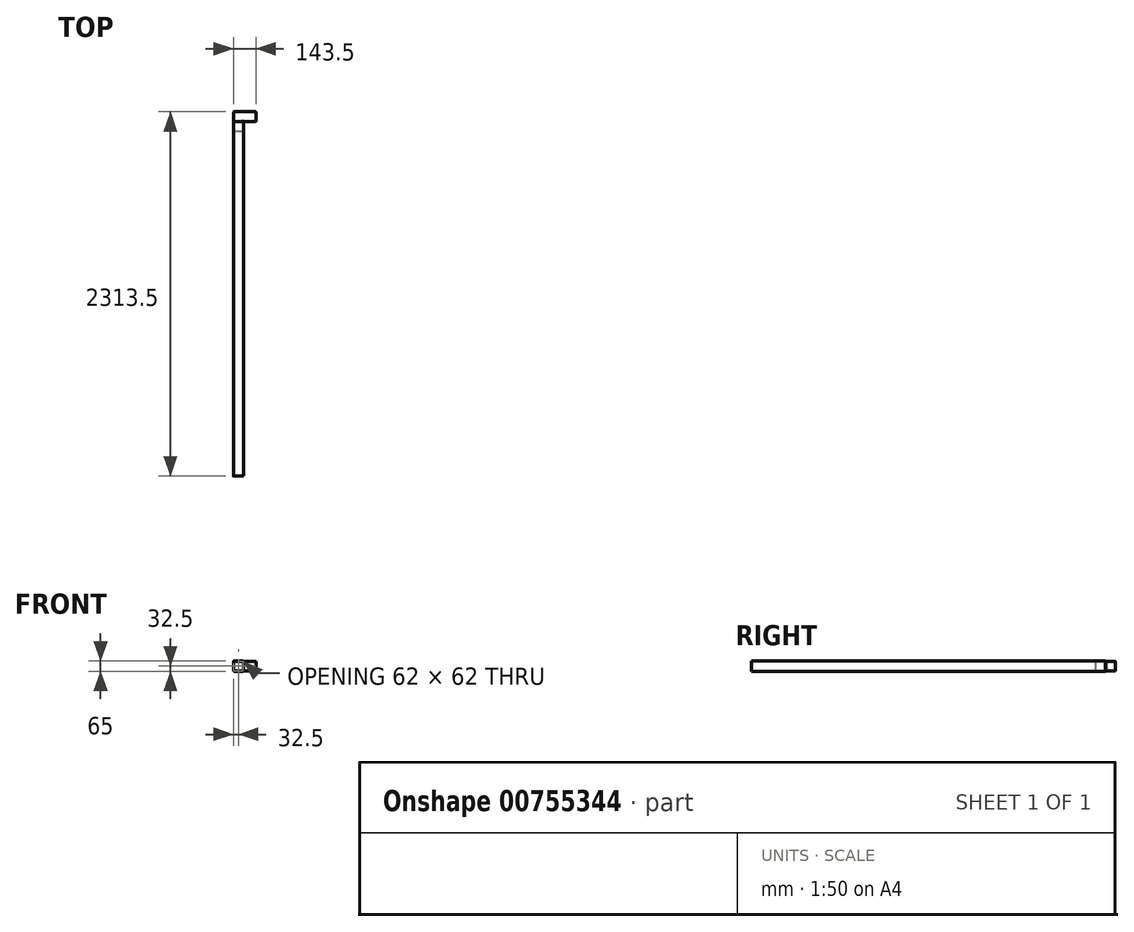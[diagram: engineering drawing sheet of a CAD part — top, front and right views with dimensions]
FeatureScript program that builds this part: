
annotation { "Feature Type Name" : "Feature", "Feature Type Description" : "" }
export const myFeature = defineFeature(function(context is Context, id is Id, definition is map)
    precondition{}
    {
        {
            assignVariable(context, id + "F0", {"name" : "T", "anyValue" : 1.5});
        }
        {
            assignVariable(context, id + "F1", {"name" : "R", "anyValue" : 5});
        }
        {
            var Q0;
            Q0=qCreatedBy(makeId("Front.planeOp"),FACE);
            var sketch = newSketch(context, id + "F2", { "sketchPlane" : qUnion([Q0])});
            skLineSegment(sketch, "E0.bottom", {"start": v(27.5, 32.5) * mm, "end": v(-27.5, 32.5) * mm});
            skLineSegment(sketch, "E0.top", {"start": v(27.5, -32.5) * mm, "end": v(-27.5, -32.5) * mm});
            skLineSegment(sketch, "E0.left", {"start": v(32.5, 27.5) * mm, "end": v(32.5, -27.5) * mm});
            skLineSegment(sketch, "E0.right", {"start": v(-32.5, 27.5) * mm, "end": v(-32.5, -27.5) * mm});
            skPoint(sketch, "E0.middle", {"position": v(0, 0) * mm});
            skPoint(sketch, "E1.visualSharp", {"position": v(-32.5, 32.5) * mm});
            skArc(sketch, "E1.filletArc", {"start": v(-27.5, 32.5) * mm, "mid": v(-31.04, 31.04) * mm, "end": v(-32.5, 27.5) * mm});
            skPoint(sketch, "E2.visualSharp", {"position": v(32.5, 32.5) * mm});
            skArc(sketch, "E2.filletArc", {"start": v(32.5, 27.5) * mm, "mid": v(31.04, 31.04) * mm, "end": v(27.5, 32.5) * mm});
            skPoint(sketch, "E3.visualSharp", {"position": v(32.5, -32.5) * mm});
            skArc(sketch, "E3.filletArc", {"start": v(27.5, -32.5) * mm, "mid": v(31.04, -31.04) * mm, "end": v(32.5, -27.5) * mm});
            skPoint(sketch, "E4.visualSharp", {"position": v(-32.5, -32.5) * mm});
            skArc(sketch, "E4.filletArc", {"start": v(-32.5, -27.5) * mm, "mid": v(-31.04, -31.04) * mm, "end": v(-27.5, -32.5) * mm});
            skPoint(sketch, "E5.visualSharp", {"position": v(-29.5, 29.5) * mm});
            skArc(sketch, "E6.0", {"start": v(31, 27.5) * mm, "mid": v(29.97, 29.97) * mm, "end": v(27.5, 31) * mm});
            skLineSegment(sketch, "E6.1", {"start": v(31, 27.5) * mm, "end": v(31, -27.5) * mm});
            skLineSegment(sketch, "E6.2", {"start": v(27.5, 31) * mm, "end": v(-27.5, 31) * mm});
            skArc(sketch, "E6.3", {"start": v(27.5, -31) * mm, "mid": v(29.97, -29.97) * mm, "end": v(31, -27.5) * mm});
            skArc(sketch, "E6.4", {"start": v(-27.5, 31) * mm, "mid": v(-29.97, 29.97) * mm, "end": v(-31, 27.5) * mm});
            skLineSegment(sketch, "E6.5", {"start": v(-31, 27.5) * mm, "end": v(-31, -27.5) * mm});
            skArc(sketch, "E6.6", {"start": v(-31, -27.5) * mm, "mid": v(-29.97, -29.97) * mm, "end": v(-27.5, -31) * mm});
            skLineSegment(sketch, "E6.7", {"start": v(27.5, -31) * mm, "end": v(-27.5, -31) * mm});
            skSolve(sketch);
        }
        {
            var Q0;
            Q0=makeQuery(id+"F2.imprint","IMPRINT",FACE,{"disambiguationData":[TD([[makeQuery(id+"F2.imprint","IMPRINT",EDGE,{"derivedFrom":sQuery(id+"F2.wireOp",EDGE,"E0.bottom")}),1.0]])]});
            extrude(context, id + "F3", {"entities" : qUnion([Q0]), "depth" : 2250 * mm, "offsetDistance" : 25 * mm});
        }
        {
            var Q0;
            Q0=makeQuery(id+"F2.imprint","IMPRINT",FACE,{"disambiguationData":[TD([[makeQuery(id+"F2.imprint","IMPRINT",EDGE,{"derivedFrom":sQuery(id+"F2.wireOp",EDGE,"E6.0")}),1.0]])]});
            extrude(context, id + "F4", {"entities" : qUnion([Q0]), "depth" : (130 - (2 * getVariable(context, 'T'))) * mm, "offsetDistance" : 25 * mm, "symmetric" : true});
        }
        {
            var Q0;
            Q0=makeQuery(id+"F4.opExtrude","SWEPT_FACE",FACE,{"disambiguationData":[OSD([sQuery(id+"F2.wireOp",EDGE,"E6.1")])]});
            var sketch = newSketch(context, id + "F5", { "sketchPlane" : qUnion([Q0])});
            skLineSegment(sketch, "E7.0", {"start": v(0, 27.5) * mm, "end": v(0, -27.5) * mm});
            skLineSegment(sketch, "E8.0", {"start": v(63.5, 27.5) * mm, "end": v(63.5, -27.5) * mm});
            skLineSegment(sketch, "E9", {"start": v(0, 0) * mm, "end": v(63.5, 0) * mm, "construction": true});
            skPoint(sketch, "E10", {"position": v(1.5, 0) * mm});
            skLineSegment(sketch, "E11", {"start": v(1.5, 0) * mm, "end": v(63.5, 0) * mm});
            skPoint(sketch, "E12", {"position": v(32.5, 0) * mm});
            skPoint(sketch, "E13.0", {"position": v(63.5, 31) * mm});
            skLineSegment(sketch, "E14.bottom", {"start": v(63.5, 31) * mm, "end": v(1.5, 31) * mm});
            skLineSegment(sketch, "E14.top", {"start": v(63.5, -31) * mm, "end": v(1.5, -31) * mm});
            skLineSegment(sketch, "E14.left", {"start": v(63.5, 31) * mm, "end": v(63.5, -31) * mm});
            skLineSegment(sketch, "E14.right", {"start": v(1.5, 31) * mm, "end": v(1.5, -31) * mm});
            skSolve(sketch);
        }
        {
            var Q0;
            {var subQ0=sQuery(id+"F5.wireOp",EDGE,"E14.bottom");Q0=makeQuery(id+"F5.imprint","IMPRINT",FACE,{"disambiguationData":[TD([[makeQuery(id+"F5.imprint","IMPRINT",EDGE,{"derivedFrom":subQ0}),1.0]])]});}
            var Q1;
            {var subQ0=sQuery(id+"F5.wireOp",EDGE,"E11");Q1=makeQuery(id+"F5.imprint","IMPRINT",FACE,{"disambiguationData":[TD([[makeQuery(id+"F5.imprint","IMPRINT",EDGE,{"derivedFrom":subQ0}),1.0]])]});}
            var Q2;
            {var subQ0=sQuery(id+"F5.wireOp",EDGE,"E11");Q2=makeQuery(id+"F5.imprint","IMPRINT",FACE,{"disambiguationData":[TD([[makeQuery(id+"F5.imprint","IMPRINT",EDGE,{"derivedFrom":subQ0}),-1.0]])]});}
            var Q3;
            {var subQ0=sQuery(id+"F5.wireOp",EDGE,"E14.top");Q3=makeQuery(id+"F5.imprint","IMPRINT",FACE,{"disambiguationData":[TD([[makeQuery(id+"F5.imprint","IMPRINT",EDGE,{"derivedFrom":subQ0}),-1.0]])]});}
            extrude(context, id + "F6", {"entities" : qUnion([Q0, Q1, Q2, Q3]), "operationType" : NewBodyOperationType.ADD, "oppositeDirection" : true, "depth" : 25 * mm, "offsetDistance" : 25 * mm});
        }
        {
            var Q0;
            Q0=makeQuery(id+"F6.boolean.opBoolean","MERGE",FACE,{"derivedFrom":[makeQuery(id+"F4.opExtrude","SWEPT_FACE",FACE,{"disambiguationData":[OSD([sQuery(id+"F2.wireOp",EDGE,"E6.1")])]}),makeQuery(id+"F6.opExtrude","CAP_FACE",FACE,{"disambiguationData":[OSD([sQuery(id+"F5.wireOp",EDGE,"E14.bottom"),sQuery(id+"F5.wireOp",EDGE,"E14.top"),sQuery(id+"F5.wireOp",EDGE,"E14.left"),sQuery(id+"F5.wireOp",EDGE,"E14.right")])],"isStart":true})]});
            var sketch = newSketch(context, id + "F7", { "sketchPlane" : qUnion([Q0])});
            skLineSegment(sketch, "E15.bottom", {"start": v(1.5, 31) * mm, "end": v(63.5, 31) * mm});
            skLineSegment(sketch, "E15.top", {"start": v(1.5, -31) * mm, "end": v(63.5, -31) * mm});
            skLineSegment(sketch, "E15.left", {"start": v(1.5, 31) * mm, "end": v(1.5, -31) * mm});
            skLineSegment(sketch, "E15.right", {"start": v(63.5, 31) * mm, "end": v(63.5, -31) * mm});
            skSolve(sketch);
        }
        {
            var Q0;
            {var subQ4=sQuery(id+"F7.wireOp",EDGE,"E15.bottom");Q0=makeQuery(id+"F7.imprint","IMPRINT",FACE,{"disambiguationData":[TD([[makeQuery(id+"F7.imprint","IMPRINT",EDGE,{"derivedFrom":subQ4}),1.0]])]});}
            var Q1;
            {var subQ0=sQuery(id+"F7.wireOp",EDGE,"E15.left");var subQ1=sQuery(id+"F2.wireOp",EDGE,"E6.1");var subQ2=makeQuery(id+"F4.opExtrude","SWEPT_EDGE",EDGE,{"disambiguationData":[OSD([sQuery(id+"F2.wireOp",EDGE,"E6.0"),subQ1])]});var subQ3=makeQuery(id+"F7.imprint","INTERSECT",VERTEX,{"derivedFrom":[subQ2,subQ0]});Q1=makeQuery(id+"F7.imprint","IMPRINT",FACE,{"disambiguationData":[TD([[makeQuery(id+"F7.imprint","IMPRINT",EDGE,{"disambiguationData":[TD([[subQ3,-1.0]])],"derivedFrom":subQ0}),1.0]])]});}
            var Q2;
            {var subQ0=sQuery(id+"F7.wireOp",EDGE,"E15.top");Q2=makeQuery(id+"F7.imprint","IMPRINT",FACE,{"disambiguationData":[TD([[makeQuery(id+"F7.imprint","IMPRINT",EDGE,{"derivedFrom":subQ0}),-1.0]])]});}
            extrude(context, id + "F8", {"entities" : qUnion([Q0, Q1, Q2]), "operationType" : NewBodyOperationType.ADD, "depth" : 80 * mm, "offsetDistance" : 25 * mm});
        }
        {
            var Q0;
            Q0=makeQuery(id+"F8.boolean.opBoolean","MERGE",EDGE,{"derivedFrom":[makeQuery(id+"F6.boolean.opBoolean","MERGE",EDGE,{"derivedFrom":[makeQuery(id+"F4.opExtrude","CAP_EDGE",EDGE,{"disambiguationData":[OSD([sQuery(id+"F2.wireOp",EDGE,"E6.2")])],"isStart":true}),makeQuery(id+"F6.opExtrude","SWEPT_EDGE",EDGE,{"disambiguationData":[OSD([sQuery(id+"F5.wireOp",EDGE,"E14.bottom"),sQuery(id+"F5.wireOp",EDGE,"E14.left")])]})]}),makeQuery(id+"F8.opExtrude","SWEPT_EDGE",EDGE,{"disambiguationData":[OSD([sQuery(id+"F7.wireOp",EDGE,"E15.bottom"),sQuery(id+"F7.wireOp",EDGE,"E15.right")])]})]});
            var Q1;
            Q1=makeQuery(id+"F8.boolean.opBoolean","MERGE",EDGE,{"derivedFrom":[makeQuery(id+"F6.opExtrude","SWEPT_EDGE",EDGE,{"disambiguationData":[OSD([sQuery(id+"F5.wireOp",EDGE,"E14.bottom"),sQuery(id+"F5.wireOp",EDGE,"E14.right")])]}),makeQuery(id+"F8.opExtrude","SWEPT_EDGE",EDGE,{"disambiguationData":[OSD([sQuery(id+"F7.wireOp",EDGE,"E15.bottom"),sQuery(id+"F7.wireOp",EDGE,"E15.left")])]})]});
            var Q2;
            Q2=makeQuery(id+"F8.boolean.opBoolean","MERGE",EDGE,{"derivedFrom":[makeQuery(id+"F6.opExtrude","SWEPT_EDGE",EDGE,{"disambiguationData":[OSD([sQuery(id+"F5.wireOp",EDGE,"E14.top"),sQuery(id+"F5.wireOp",EDGE,"E14.right")])]}),makeQuery(id+"F8.opExtrude","SWEPT_EDGE",EDGE,{"disambiguationData":[OSD([sQuery(id+"F7.wireOp",EDGE,"E15.top"),sQuery(id+"F7.wireOp",EDGE,"E15.left")])]})]});
            var Q3;
            Q3=makeQuery(id+"F8.opExtrude","CAP_EDGE",EDGE,{"disambiguationData":[OSD([sQuery(id+"F7.wireOp",EDGE,"E15.left")])],"isStart":false});
            var Q4;
            Q4=makeQuery(id+"F8.opExtrude","CAP_EDGE",EDGE,{"disambiguationData":[OSD([sQuery(id+"F7.wireOp",EDGE,"E15.top")])],"isStart":false});
            var Q5;
            Q5=makeQuery(id+"F8.opExtrude","CAP_EDGE",EDGE,{"disambiguationData":[OSD([sQuery(id+"F7.wireOp",EDGE,"E15.right")])],"isStart":false});
            var Q6;
            Q6=makeQuery(id+"F8.opExtrude","CAP_EDGE",EDGE,{"disambiguationData":[OSD([sQuery(id+"F7.wireOp",EDGE,"E15.bottom")])],"isStart":false});
            var Q7;
            Q7=makeQuery(id+"F8.opExtrude","SWEPT_EDGE",EDGE,{"disambiguationData":[OSD([sQuery(id+"F7.wireOp",EDGE,"E15.top"),sQuery(id+"F7.wireOp",EDGE,"E15.right")])]});
            var Q8;
            Q8=makeQuery(id+"F4.opExtrude","CAP_EDGE",EDGE,{"disambiguationData":[OSD([sQuery(id+"F2.wireOp",EDGE,"E6.7")])],"isStart":true});
            fillet(context, id + "F9", {"entities" : qUnion([Q0, Q1, Q2, Q3, Q4, Q5, Q6, Q7, Q8]), "radius" : (getVariable(context, 'R') - getVariable(context, 'T')) * mm, "tangentPropagation" : true, "allowEdgeOverflow" : false});
        }
    });
